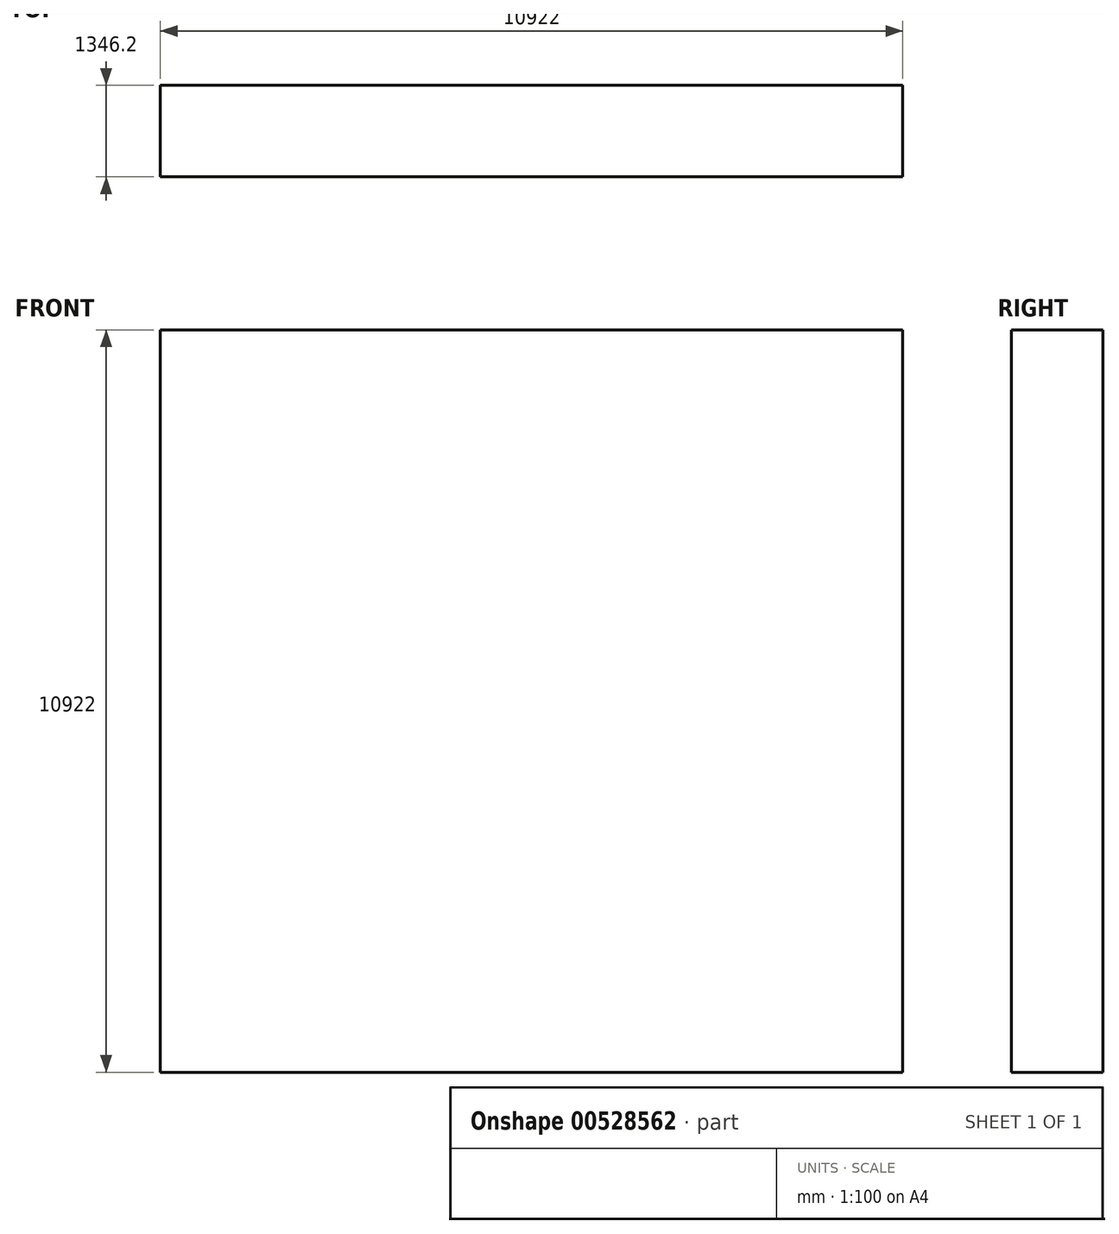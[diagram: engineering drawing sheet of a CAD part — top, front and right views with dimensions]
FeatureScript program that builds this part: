
annotation { "Feature Type Name" : "Feature", "Feature Type Description" : "" }
export const myFeature = defineFeature(function(context is Context, id is Id, definition is map)
    precondition{}
    {
        {
            var Q0;
            Q0=qCreatedBy(makeId("Front.planeOp"),FACE);
            var sketch = newSketch(context, id + "F0", { "sketchPlane" : qUnion([Q0])});
            skLineSegment(sketch, "E0.bottom", {"start": v(-5461, 5461) * mm, "end": v(5461, 5461) * mm});
            skLineSegment(sketch, "E0.top", {"start": v(-5461, -5461) * mm, "end": v(5461, -5461) * mm});
            skLineSegment(sketch, "E0.left", {"start": v(-5461, 5461) * mm, "end": v(-5461, -5461) * mm});
            skLineSegment(sketch, "E0.right", {"start": v(5461, 5461) * mm, "end": v(5461, -5461) * mm});
            skSolve(sketch);
        }
        {
            var Q0;
            Q0 = qSketchRegion(id + "F0", true);
            extrude(context, id + "F1", {"entities" : qUnion([Q0]), "depth" : 1346.2 * mm, "offsetDistance" : 25.4 * mm});
        }
    });
